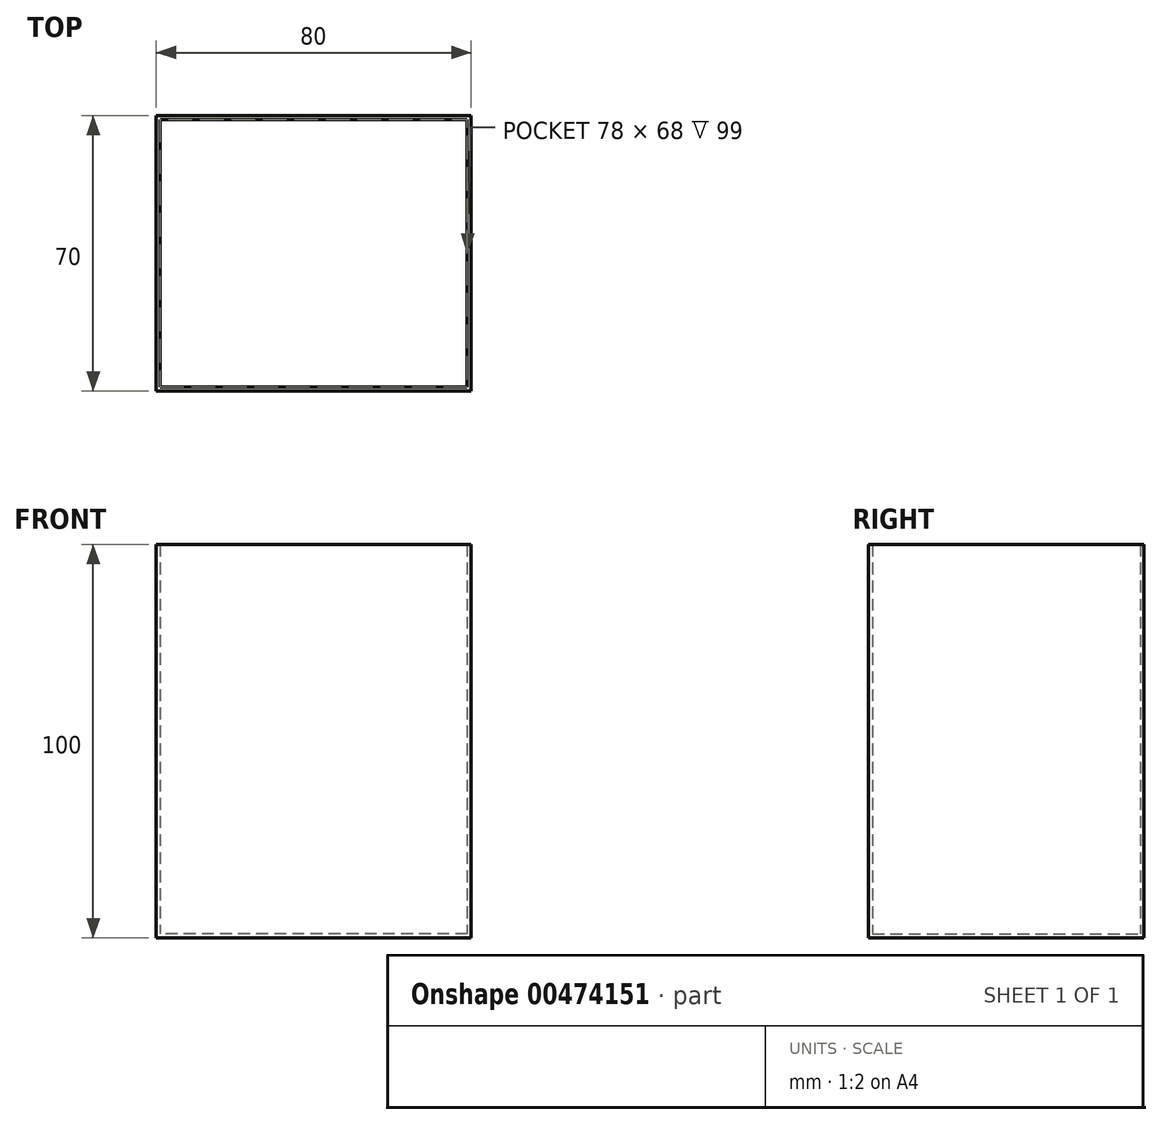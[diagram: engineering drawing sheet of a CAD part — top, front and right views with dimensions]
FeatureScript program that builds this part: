
annotation { "Feature Type Name" : "Feature", "Feature Type Description" : "" }
export const myFeature = defineFeature(function(context is Context, id is Id, definition is map)
    precondition{}
    {
        {
            var Q0;
            Q0=qCreatedBy(makeId("Front.planeOp"),FACE);
            var sketch = newSketch(context, id + "F0", { "sketchPlane" : qUnion([Q0])});
            skLineSegment(sketch, "E0.bottom", {"start": v(40, 50) * mm, "end": v(-40, 50) * mm});
            skLineSegment(sketch, "E0.top", {"start": v(40, -50) * mm, "end": v(-40, -50) * mm});
            skLineSegment(sketch, "E0.left", {"start": v(40, 50) * mm, "end": v(40, -50) * mm});
            skLineSegment(sketch, "E0.right", {"start": v(-40, 50) * mm, "end": v(-40, -50) * mm});
            skPoint(sketch, "E0.middle", {"position": v(0, 0) * mm});
            skSolve(sketch);
        }
        {
            var Q0;
            Q0 = qSketchRegion(id + "F0", true);
            extrude(context, id + "F1", {"entities" : qUnion([Q0]), "endBound" : BoundingType.SYMMETRIC, "depth" : 70 * mm});
        }
        {
            var Q0;
            Q0=makeQuery(id+"F1.opExtrude","SWEPT_FACE",FACE,{"disambiguationData":[OSD([sQuery(id+"F0.wireOp",EDGE,"E0.bottom")])]});
            shell(context, id + "F2", {"entities" : qUnion([Q0]), "thickness" : 1 * mm});
        }
    });
